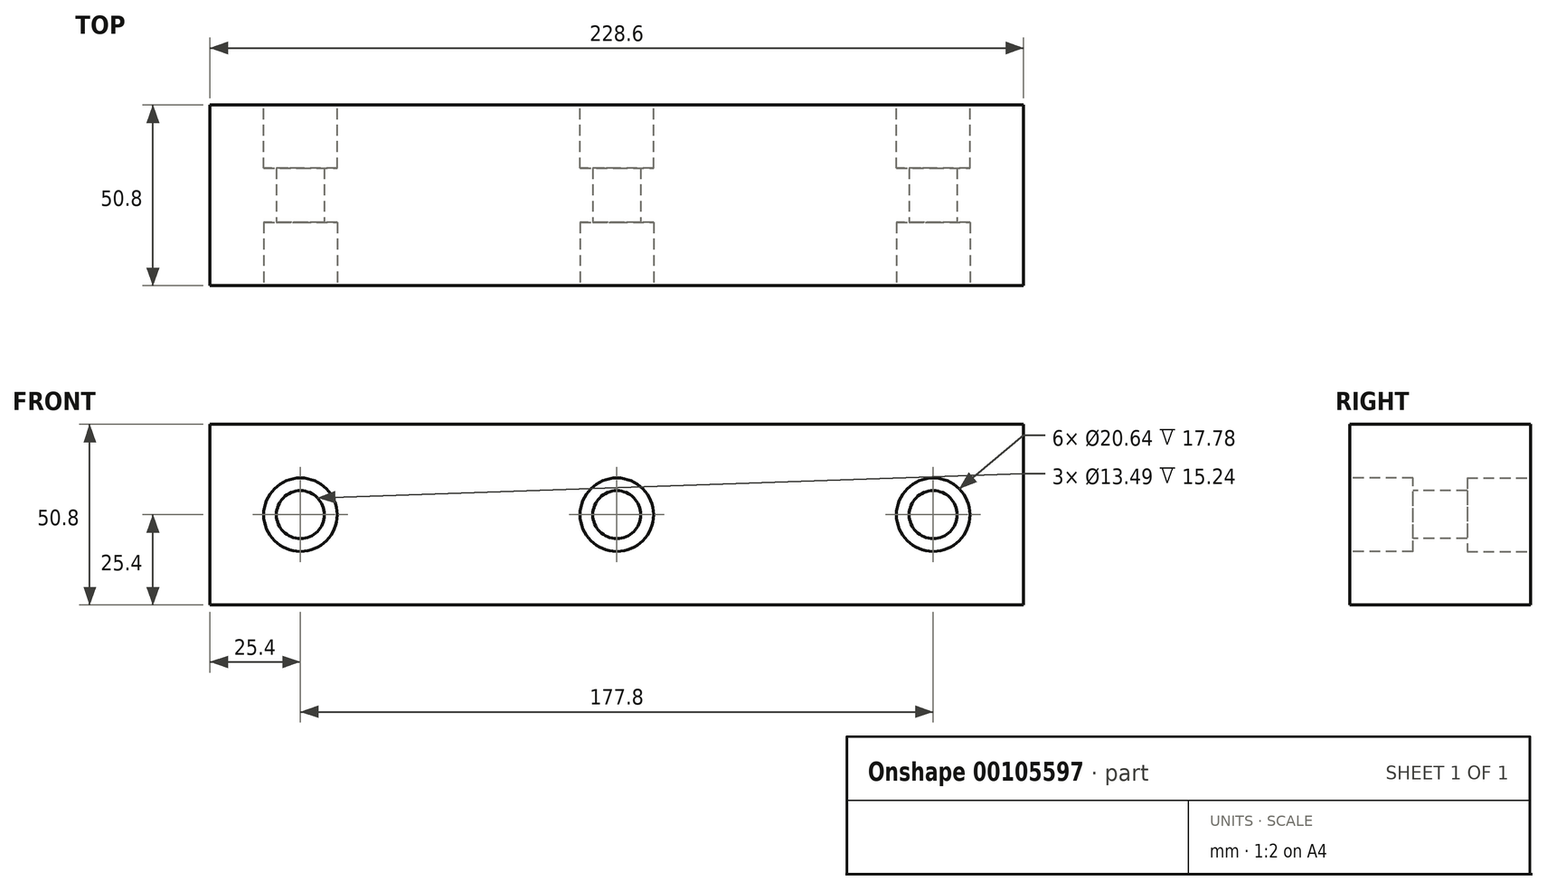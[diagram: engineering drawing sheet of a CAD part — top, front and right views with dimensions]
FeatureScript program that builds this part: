
annotation { "Feature Type Name" : "Feature", "Feature Type Description" : "" }
export const myFeature = defineFeature(function(context is Context, id is Id, definition is map)
    precondition{}
    {
        {
            var Q0;
            Q0=qCreatedBy(makeId("Front.planeOp"),FACE);
            var sketch = newSketch(context, id + "F0", { "sketchPlane" : qUnion([Q0])});
            skLineSegment(sketch, "E0.bottom", {"start": v(-114.3, 25.4) * mm, "end": v(114.3, 25.4) * mm});
            skLineSegment(sketch, "E0.top", {"start": v(-114.3, -25.4) * mm, "end": v(114.3, -25.4) * mm});
            skLineSegment(sketch, "E0.left", {"start": v(-114.3, 25.4) * mm, "end": v(-114.3, -25.4) * mm});
            skLineSegment(sketch, "E0.right", {"start": v(114.3, 25.4) * mm, "end": v(114.3, -25.4) * mm});
            skPoint(sketch, "E0.middle", {"position": v(0, 0) * mm});
            skSolve(sketch);
        }
        {
            var Q0;
            Q0=makeQuery(id+"F0.imprint","IMPRINT",FACE,{"disambiguationData":[TD([[makeQuery(id+"F0.imprint","IMPRINT",EDGE,{"derivedFrom":sQuery(id+"F0.wireOp",EDGE,"E0.bottom")}),-1.0]])]});
            extrude(context, id + "F1", {"entities" : qUnion([Q0]), "depth" : 50.8 * mm});
        }
        {
            var Q0;
            Q0=makeQuery(id+"F1.opExtrude","CAP_FACE",FACE,{"disambiguationData":[OSD([sQuery(id+"F0.wireOp",EDGE,"E0.bottom"),sQuery(id+"F0.wireOp",EDGE,"E0.top"),sQuery(id+"F0.wireOp",EDGE,"E0.left"),sQuery(id+"F0.wireOp",EDGE,"E0.right")])],"isStart":false});
            var sketch = newSketch(context, id + "F2", { "sketchPlane" : qUnion([Q0])});
            skPoint(sketch, "E1", {"position": v(-88.9, 0) * mm});
            skPoint(sketch, "E2", {"position": v(0, 0) * mm});
            skPoint(sketch, "E3", {"position": v(88.9, 0) * mm});
            skSolve(sketch);
        }
        {
            var Q0;
            Q0=sQuery(id+"F2.wireOp",VERTEX,"E1");
            var Q1;
            Q1=sQuery(id+"F2.wireOp",VERTEX,"E2");
            var Q2;
            Q2=sQuery(id+"F2.wireOp",VERTEX,"E3");
            var Q3;
            Q3=makeQuery(id+"F1.opExtrude","SWEPT_BODY",BODY,{"disambiguationData":[OSD([sQuery(id+"F0.wireOp",EDGE,"E0.bottom"),sQuery(id+"F0.wireOp",EDGE,"E0.top"),sQuery(id+"F0.wireOp",EDGE,"E0.left"),sQuery(id+"F0.wireOp",EDGE,"E0.right")])]});
            hole(context, id + "F3", {"style" : HoleStyle.C_BORE, "endStyle" : HoleEndStyle.THROUGH, "holeDiameter" : 13.5 * mm, "cBoreDiameter" : 20.64 * mm, "cBoreDepth" : 17.78 * mm, "locations" : qUnion([Q0, Q1, Q2]), "scope" : qUnion([Q3]), "isTappedThrough" : true});
        }
        {
            var Q0;
            Q0=makeQuery(id+"F0.imprint","IMPRINT",FACE,{"disambiguationData":[TD([[makeQuery(id+"F0.imprint","IMPRINT",EDGE,{"derivedFrom":sQuery(id+"F0.wireOp",EDGE,"E0.bottom")}),-1.0]])]});
            var sketch = newSketch(context, id + "F4", { "sketchPlane" : qUnion([Q0])});
            skPoint(sketch, "E4", {"position": v(88.9, 0) * mm});
            skPoint(sketch, "E5", {"position": v(0, 0) * mm});
            skPoint(sketch, "E6", {"position": v(-88.9, 0) * mm});
            skSolve(sketch);
        }
        {
            var Q0;
            Q0=sQuery(id+"F4.wireOp",VERTEX,"E4");
            var Q1;
            Q1=sQuery(id+"F4.wireOp",VERTEX,"E5");
            var Q2;
            Q2=sQuery(id+"F4.wireOp",VERTEX,"E6");
            var Q3;
            Q3=makeQuery(id+"F1.opExtrude","SWEPT_BODY",BODY,{"disambiguationData":[OSD([sQuery(id+"F0.wireOp",EDGE,"E0.bottom"),sQuery(id+"F0.wireOp",EDGE,"E0.top"),sQuery(id+"F0.wireOp",EDGE,"E0.left"),sQuery(id+"F0.wireOp",EDGE,"E0.right")])]});
            hole(context, id + "F5", {"style" : HoleStyle.C_BORE, "endStyle" : HoleEndStyle.BLIND, "oppositeDirection" : true, "holeDiameter" : 13.5 * mm, "cBoreDiameter" : 20.64 * mm, "cBoreDepth" : 17.78 * mm, "holeDepth" : 25.4 * mm, "startFromSketch" : true, "locations" : qUnion([Q0, Q1, Q2]), "scope" : qUnion([Q3])});
        }
    });
